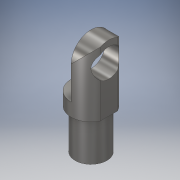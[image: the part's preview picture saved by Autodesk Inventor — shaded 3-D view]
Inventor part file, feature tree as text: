
AUTODESK INVENTOR PART (.ipt)
format: ipt  version: 2018 (Build 220112000, 112)  size: 158,208 bytes
history: native  units: in
note: dims shown in document units (in); Inventor stores cm internally (conversion verified against a paired STEP export)
features: sketch x7, extrude x5, hole x2
ambient origin geometry x8: Origin, YZ Plane, XZ Plane, XY Plane, X Axis, Y Axis, Z Axis, Center Point
bodies: Solid1 (feature_tree)
feature tree (14):
  extrude  "Extrusion1"  Depth=0.375in TaperAngle=0.0deg
  hole  "Hole1"  [1 undecoded]
  extrude  "Extrusion2"  Depth=0.5in TaperAngle=0.0deg
  extrude  "Extrusion3"  Depth=1.0in TaperAngle=0.0deg
  hole  "Hole2"  [1 undecoded]
  extrude  "Extrusion4"  [1 undecoded]
  extrude  "Extrusion5"  [1 undecoded]
  sketch  "Sketch1"  dims[d0=0.375in d1=0.5in d2=0.0in]
  sketch  "Sketch2"  dims[d3=0.196in d4=0.5in d5=0.375in d6=0.25in d7=0.5635in d8=0.75in d9=0.8108in d10=0.375in]
  sketch  "Sketch3"  dims[d11=0.5in d12=0.0in d13=0.5in d14=0.0in]
  sketch  "Sketch4"  dims[d15=0.266in d16=0.5in d17=0.507in d18=0.25in d19=0.5635in d20=0.75in d21=0.8108in d22=1.0in d23=0.0in]
  sketch  "Sketch5"  dims[d24=0.375in d25=0.3in]
  sketch  "Sketch6"  dims[d26=0.375in d27=0.0in]
  sketch  "Sketch7"
note: 4 required parameter values undecoded (feature->parameter linkage not recoverable at this tier; creation-order binding heuristic only, values carry confidence <= 0.55)
